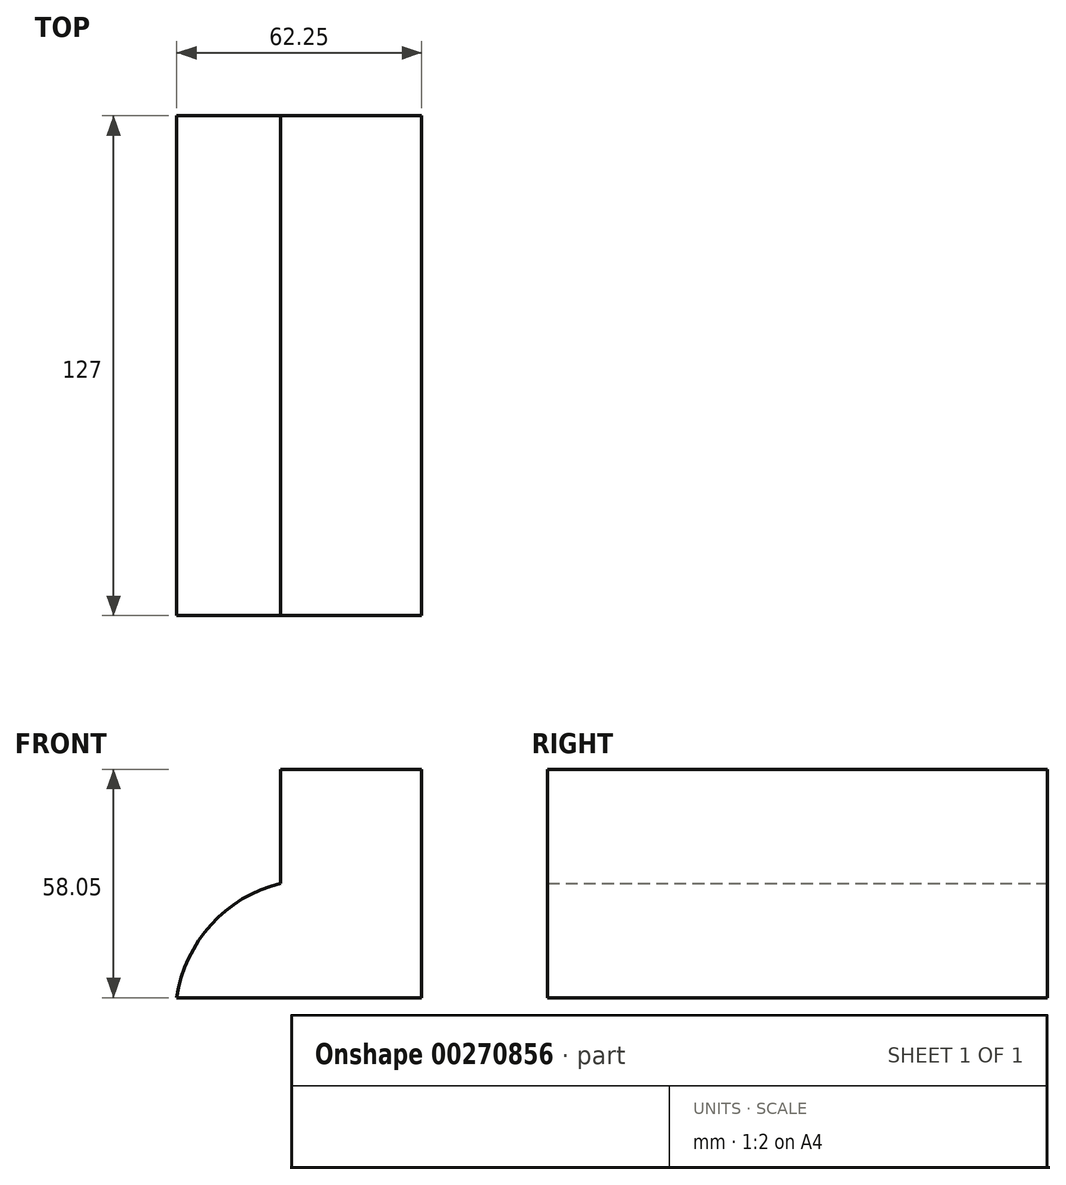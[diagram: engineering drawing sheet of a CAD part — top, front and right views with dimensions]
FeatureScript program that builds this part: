
annotation { "Feature Type Name" : "Feature", "Feature Type Description" : "" }
export const myFeature = defineFeature(function(context is Context, id is Id, definition is map)
    precondition{}
    {
        {
            var Q0;
            Q0=qCreatedBy(makeId("Front.planeOp"),FACE);
            var sketch = newSketch(context, id + "F0", { "sketchPlane" : qUnion([Q0])});
            skLineSegment(sketch, "E0", {"start": v(-47.55, 66.45) * mm, "end": v(-11.65, 66.45) * mm});
            skLineSegment(sketch, "E1", {"start": v(-11.65, 66.45) * mm, "end": v(-11.65, 8.4) * mm});
            skLineSegment(sketch, "E2", {"start": v(-11.65, 8.4) * mm, "end": v(-73.9, 8.4) * mm});
            skLineSegment(sketch, "E3", {"start": v(-47.55, 66.45) * mm, "end": v(-47.55, 37.43) * mm});
            skArc(sketch, "E4", {"start": v(-47.55, 37.43) * mm, "mid": v(-65.14, 26.93) * mm, "end": v(-73.9, 8.4) * mm});
            skSolve(sketch);
        }
        {
            var Q0;
            Q0 = qSketchRegion(id + "F0", true);
            extrude(context, id + "F1", {"entities" : qUnion([Q0]), "depth" : 127 * mm});
        }
    });
